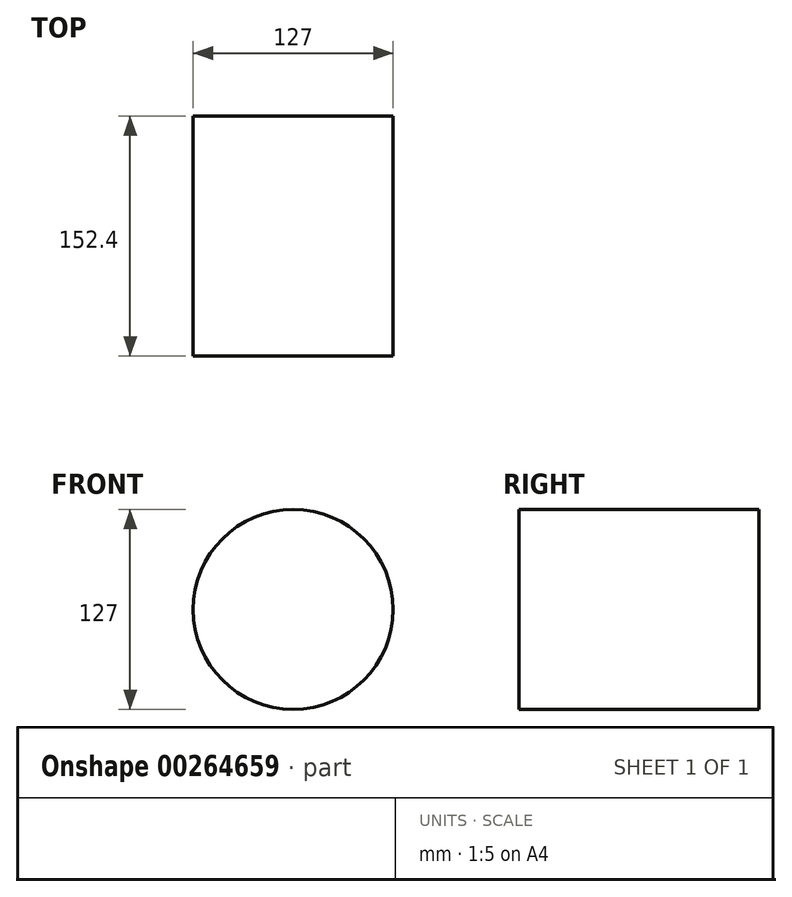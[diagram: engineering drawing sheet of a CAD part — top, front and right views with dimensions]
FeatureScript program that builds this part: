
annotation { "Feature Type Name" : "Feature", "Feature Type Description" : "" }
export const myFeature = defineFeature(function(context is Context, id is Id, definition is map)
    precondition{}
    {
        {
            var Q0;
            Q0=qCreatedBy(makeId("Front.planeOp"),FACE);
            var sketch = newSketch(context, id + "F0", { "sketchPlane" : qUnion([Q0])});
            skCircle(sketch, "E0", {"center": v(0, 0) * mm, "radius": 63.5 * mm});
            skSolve(sketch);
        }
        {
            var Q0;
            Q0=makeQuery(id+"F0.imprint","IMPRINT",FACE,{"disambiguationData":[TD([[makeQuery(id+"F0.imprint","IMPRINT",EDGE,{"derivedFrom":sQuery(id+"F0.wireOp",EDGE,"E0")}),1.0]])]});
            extrude(context, id + "F1", {"entities" : qUnion([Q0]), "depth" : 152.4 * mm});
        }
    });
